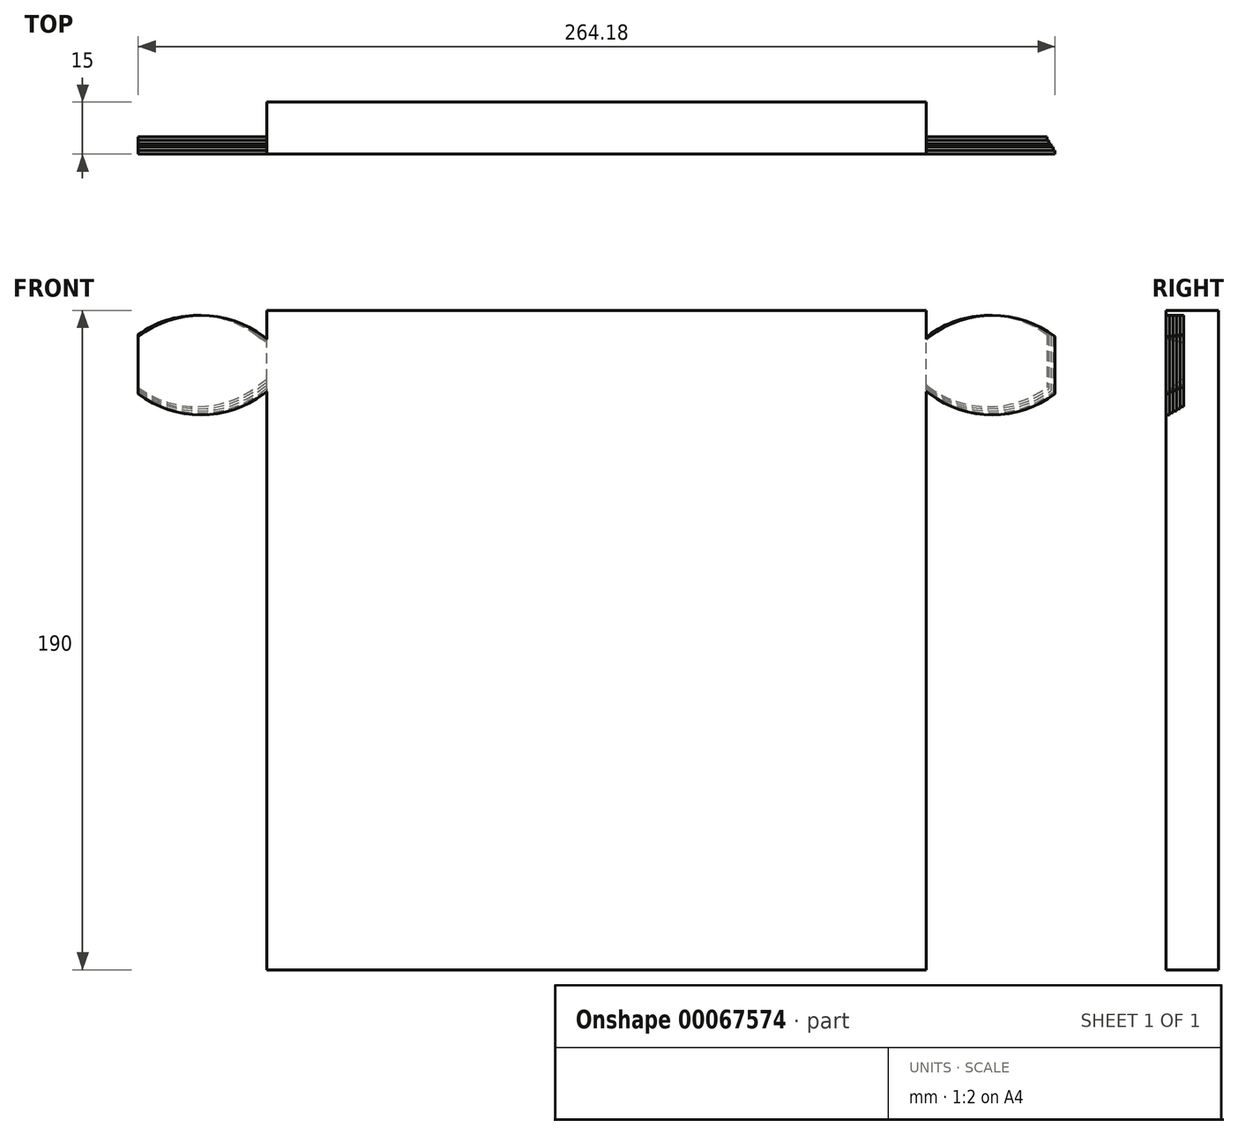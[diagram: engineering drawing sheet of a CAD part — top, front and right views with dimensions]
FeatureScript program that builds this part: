
annotation { "Feature Type Name" : "Feature", "Feature Type Description" : "" }
export const myFeature = defineFeature(function(context is Context, id is Id, definition is map)
    precondition{}
    {
        {
            var Q0;
            Q0=qCreatedBy(makeId("Front.planeOp"),FACE);
            var sketch = newSketch(context, id + "F0", { "sketchPlane" : qUnion([Q0])});
            skLineSegment(sketch, "E0.bottom", {"start": v(95, -95) * mm, "end": v(-95, -95) * mm});
            skLineSegment(sketch, "E0.top", {"start": v(95, 95) * mm, "end": v(-95, 95) * mm});
            skLineSegment(sketch, "E0.left", {"start": v(95, -95) * mm, "end": v(95, 95) * mm});
            skLineSegment(sketch, "E0.right", {"start": v(-95, -95) * mm, "end": v(-95, 95) * mm});
            skPoint(sketch, "E0.middle", {"position": v(0, 0) * mm});
            skSolve(sketch);
        }
        {
            var Q0;
            Q0=makeQuery(id+"F0.imprint","IMPRINT",FACE,{"disambiguationData":[TD([[makeQuery(id+"F0.imprint","IMPRINT",EDGE,{"derivedFrom":sQuery(id+"F0.wireOp",EDGE,"E0.bottom")}),-1.0]])]});
            extrude(context, id + "F1", {"entities" : qUnion([Q0]), "oppositeDirection" : true, "depth" : 15 * mm});
        }
        {
            var Q0;
            Q0=makeQuery(id+"F1.opExtrude","CAP_FACE",FACE,{"disambiguationData":[OSD([sQuery(id+"F0.wireOp",EDGE,"E0.bottom"),sQuery(id+"F0.wireOp",EDGE,"E0.top"),sQuery(id+"F0.wireOp",EDGE,"E0.left"),sQuery(id+"F0.wireOp",EDGE,"E0.right")])],"isStart":true});
            var sketch = newSketch(context, id + "F2", { "sketchPlane" : qUnion([Q0])});
            skLineSegment(sketch, "E1.bottom", {"start": v(-95, -95) * mm, "end": v(95, -95) * mm, "construction": true});
            skLineSegment(sketch, "E1.top", {"start": v(-95, 95) * mm, "end": v(95, 95) * mm, "construction": true});
            skLineSegment(sketch, "E1.left", {"start": v(-95, -95) * mm, "end": v(-95, 95) * mm, "construction": true});
            skLineSegment(sketch, "E1.right", {"start": v(95, -95) * mm, "end": v(95, 95) * mm, "construction": true});
            skPoint(sketch, "E1.middle", {"position": v(0, 0) * mm});
            skLineSegment(sketch, "E2", {"start": v(0, 95) * mm, "end": v(0, -95) * mm, "construction": true});
            skLineSegment(sketch, "E3", {"start": v(-95, 88.58) * mm, "end": v(95, 88.58) * mm, "construction": true});
            skArc(sketch, "E4", {"start": v(57, 88.58) * mm, "mid": v(76, 82.17) * mm, "end": v(95, 88.58) * mm, "construction": true});
            skArc(sketch, "E5", {"start": v(57, 88.58) * mm, "mid": v(38, 95) * mm, "end": v(19, 88.58) * mm, "construction": true});
            skArc(sketch, "E6", {"start": v(-19, 88.58) * mm, "mid": v(0, 82.17) * mm, "end": v(19, 88.58) * mm, "construction": true});
            skArc(sketch, "E7", {"start": v(-19, 88.58) * mm, "mid": v(-38, 95) * mm, "end": v(-57, 88.58) * mm, "construction": true});
            skArc(sketch, "E8", {"start": v(-95, 88.58) * mm, "mid": v(-76, 82.17) * mm, "end": v(-57, 88.58) * mm, "construction": true});
            skLineSegment(sketch, "E9", {"start": v(-95, 113.5) * mm, "end": v(95, 113.5) * mm, "construction": true});
            skLineSegment(sketch, "E10", {"start": v(-95, 63.66) * mm, "end": v(95, 63.66) * mm, "construction": true});
            skLineSegment(sketch, "E11", {"start": v(0, 113.5) * mm, "end": v(95, 88.58) * mm, "construction": true});
            skLineSegment(sketch, "E12", {"start": v(0, 88.58) * mm, "end": v(95, 63.66) * mm, "construction": true});
            skArc(sketch, "E13.1.0", {"start": v(-95, 88.58) * mm, "mid": v(-114, 95) * mm, "end": v(-133, 88.58) * mm, "construction": true});
            skPoint(sketch, "E13.center", {"position": v(-95, 88.58) * mm});
            skArc(sketch, "E14.1.0", {"start": v(133, 88.58) * mm, "mid": v(114, 95) * mm, "end": v(95, 88.58) * mm, "construction": true});
            skPoint(sketch, "E14.center", {"position": v(95, 88.58) * mm});
            skLineSegment(sketch, "E15", {"start": v(-95, 0) * mm, "end": v(95, 0) * mm, "construction": true});
            skLineSegment(sketch, "E16", {"start": v(-95, -79.17) * mm, "end": v(95, -79.17) * mm, "construction": true});
            skLineSegment(sketch, "E17", {"start": v(-95, -63.33) * mm, "end": v(95, -63.33) * mm, "construction": true});
            skLineSegment(sketch, "E18", {"start": v(-95, -47.5) * mm, "end": v(95, -47.5) * mm, "construction": true});
            skLineSegment(sketch, "E19", {"start": v(-95, -31.67) * mm, "end": v(95, -31.67) * mm, "construction": true});
            skLineSegment(sketch, "E20", {"start": v(-95, -15.83) * mm, "end": v(95, -15.83) * mm, "construction": true});
            skLineSegment(sketch, "E21", {"start": v(0, 0) * mm, "end": v(95, -15.83) * mm, "construction": true});
            skLineSegment(sketch, "E22", {"start": v(0, -15.83) * mm, "end": v(95, -31.67) * mm, "construction": true});
            skLineSegment(sketch, "E23", {"start": v(0, -31.67) * mm, "end": v(95, -47.5) * mm, "construction": true});
            skLineSegment(sketch, "E24", {"start": v(0, -47.5) * mm, "end": v(95, -63.33) * mm, "construction": true});
            skLineSegment(sketch, "E25", {"start": v(0, -63.33) * mm, "end": v(95, -79.17) * mm, "construction": true});
            skLineSegment(sketch, "E26", {"start": v(0, -79.17) * mm, "end": v(95, -95) * mm, "construction": true});
            skLineSegment(sketch, "E27", {"start": v(-76, 82.17) * mm, "end": v(-38, 82.17) * mm, "construction": true});
            skPoint(sketch, "E27.endSnap0", {"position": v(-38, 95) * mm});
            skLineSegment(sketch, "E28", {"start": v(-38, 82.17) * mm, "end": v(-38, 95) * mm, "construction": true});
            skLineSegment(sketch, "E29", {"start": v(-95, 0) * mm, "end": v(-95, -15.83) * mm, "construction": true});
            skLineSegment(sketch, "E30", {"start": v(-95, -12.83) * mm, "end": v(0, -12.83) * mm, "construction": true});
            skLineSegment(sketch, "E31", {"start": v(-47.5, -12.83) * mm, "end": v(-47.5, -15.83) * mm, "construction": true});
            skLineSegment(sketch, "E32", {"start": v(-47.5, -12.83) * mm, "end": v(-47.5, 0) * mm, "construction": true});
            skLineSegment(sketch, "E33", {"start": v(-95, 79.17) * mm, "end": v(95, 79.17) * mm, "construction": true});
            skPoint(sketch, "E34", {"position": v(38, 95) * mm});
            skArc(sketch, "E35.0", {"start": v(-94.1, 89.78) * mm, "mid": v(-114, 96.5) * mm, "end": v(-133.9, 89.78) * mm});
            skArc(sketch, "E35.1", {"start": v(-94.1, 89.78) * mm, "mid": v(-76, 83.67) * mm, "end": v(-57.9, 89.78) * mm});
            skArc(sketch, "E35.2", {"start": v(-18.1, 89.78) * mm, "mid": v(-38, 96.5) * mm, "end": v(-57.9, 89.78) * mm});
            skArc(sketch, "E35.3", {"start": v(133.9, 89.78) * mm, "mid": v(114, 96.5) * mm, "end": v(94.1, 89.78) * mm});
            skArc(sketch, "E35.4", {"start": v(57.9, 89.78) * mm, "mid": v(76, 83.67) * mm, "end": v(94.1, 89.78) * mm});
            skArc(sketch, "E35.5", {"start": v(57.9, 89.78) * mm, "mid": v(38, 96.5) * mm, "end": v(18.1, 89.78) * mm});
            skArc(sketch, "E35.6", {"start": v(-18.1, 89.78) * mm, "mid": v(0, 83.67) * mm, "end": v(18.1, 89.78) * mm});
            skArc(sketch, "E36.0", {"start": v(-95.9, 87.4) * mm, "mid": v(-114, 93.5) * mm, "end": v(-132.1, 87.4) * mm});
            skArc(sketch, "E36.1", {"start": v(-95.9, 87.4) * mm, "mid": v(-76, 80.67) * mm, "end": v(-56.1, 87.4) * mm});
            skArc(sketch, "E36.2", {"start": v(-19.9, 87.4) * mm, "mid": v(-38, 93.5) * mm, "end": v(-56.1, 87.4) * mm});
            skArc(sketch, "E36.3", {"start": v(132.1, 87.4) * mm, "mid": v(114, 93.5) * mm, "end": v(95.9, 87.4) * mm});
            skArc(sketch, "E36.4", {"start": v(56.1, 87.4) * mm, "mid": v(76, 80.67) * mm, "end": v(95.9, 87.4) * mm});
            skArc(sketch, "E36.5", {"start": v(56.1, 87.4) * mm, "mid": v(38, 93.5) * mm, "end": v(19.9, 87.4) * mm});
            skArc(sketch, "E36.6", {"start": v(-19.9, 87.4) * mm, "mid": v(0, 80.67) * mm, "end": v(19.9, 87.4) * mm});
            skArc(sketch, "E37.MirrorCS", {"start": v(-94.1, 68.56) * mm, "mid": v(-114, 61.83) * mm, "end": v(-133.9, 68.56) * mm});
            skArc(sketch, "E38.MirrorCS", {"start": v(-95.9, 70.94) * mm, "mid": v(-114, 64.83) * mm, "end": v(-132.1, 70.94) * mm});
            skArc(sketch, "E39.MirrorCS", {"start": v(-94.1, 68.56) * mm, "mid": v(-76, 74.67) * mm, "end": v(-57.9, 68.56) * mm});
            skArc(sketch, "E40.MirrorCS", {"start": v(-95.9, 70.94) * mm, "mid": v(-76, 77.67) * mm, "end": v(-56.1, 70.94) * mm});
            skArc(sketch, "E41.MirrorCS", {"start": v(-18.1, 68.56) * mm, "mid": v(-38, 61.83) * mm, "end": v(-57.9, 68.56) * mm});
            skArc(sketch, "E42.MirrorCS", {"start": v(-19.9, 70.94) * mm, "mid": v(-38, 64.83) * mm, "end": v(-56.1, 70.94) * mm});
            skArc(sketch, "E43.MirrorCS", {"start": v(-18.1, 68.56) * mm, "mid": v(0, 74.67) * mm, "end": v(18.1, 68.56) * mm});
            skArc(sketch, "E44.MirrorCS", {"start": v(-19.9, 70.94) * mm, "mid": v(0, 77.67) * mm, "end": v(19.9, 70.94) * mm});
            skArc(sketch, "E45.MirrorCS", {"start": v(57.9, 68.56) * mm, "mid": v(38, 61.83) * mm, "end": v(18.1, 68.56) * mm});
            skArc(sketch, "E46.MirrorCS", {"start": v(56.1, 70.94) * mm, "mid": v(38, 64.83) * mm, "end": v(19.9, 70.94) * mm});
            skArc(sketch, "E47.MirrorCS", {"start": v(57.9, 68.56) * mm, "mid": v(76, 74.67) * mm, "end": v(94.1, 68.56) * mm});
            skArc(sketch, "E48.MirrorCS", {"start": v(56.1, 70.94) * mm, "mid": v(76, 77.67) * mm, "end": v(95.9, 70.94) * mm});
            skArc(sketch, "E49.MirrorCS", {"start": v(133.9, 68.56) * mm, "mid": v(114, 61.83) * mm, "end": v(94.1, 68.56) * mm});
            skArc(sketch, "E50.MirrorCS", {"start": v(132.1, 70.94) * mm, "mid": v(114, 64.83) * mm, "end": v(95.9, 70.94) * mm});
            skArc(sketch, "E51.0.1.0", {"start": v(56.1, 33.6) * mm, "mid": v(76, 40.33) * mm, "end": v(95.9, 33.6) * mm});
            skArc(sketch, "E51.0.1.1", {"start": v(-94.1, 31.22) * mm, "mid": v(-114, 24.5) * mm, "end": v(-133.9, 31.22) * mm});
            skArc(sketch, "E51.0.1.2", {"start": v(57.9, 52.44) * mm, "mid": v(76, 46.33) * mm, "end": v(94.1, 52.44) * mm});
            skArc(sketch, "E51.0.1.3", {"start": v(-95.9, 50.05) * mm, "mid": v(-114, 56.16) * mm, "end": v(-132.1, 50.05) * mm});
            skArc(sketch, "E51.0.1.4", {"start": v(56.1, 50.05) * mm, "mid": v(38, 56.16) * mm, "end": v(19.9, 50.05) * mm});
            skArc(sketch, "E51.0.1.5", {"start": v(-95.9, 33.6) * mm, "mid": v(-76, 40.33) * mm, "end": v(-56.1, 33.6) * mm});
            skArc(sketch, "E51.0.1.6", {"start": v(-18.1, 52.44) * mm, "mid": v(0, 46.33) * mm, "end": v(18.1, 52.44) * mm});
            skArc(sketch, "E51.0.1.7", {"start": v(132.1, 33.6) * mm, "mid": v(114, 27.5) * mm, "end": v(95.9, 33.6) * mm});
            skArc(sketch, "E51.0.1.8", {"start": v(-19.9, 50.05) * mm, "mid": v(-38, 56.16) * mm, "end": v(-56.1, 50.05) * mm});
            skArc(sketch, "E51.0.1.9", {"start": v(-94.1, 52.44) * mm, "mid": v(-76, 46.33) * mm, "end": v(-57.9, 52.44) * mm});
            skArc(sketch, "E51.0.1.10", {"start": v(-18.1, 31.22) * mm, "mid": v(-38, 24.5) * mm, "end": v(-57.9, 31.22) * mm});
            skArc(sketch, "E51.0.1.11", {"start": v(-95.9, 33.6) * mm, "mid": v(-114, 27.5) * mm, "end": v(-132.1, 33.6) * mm});
            skArc(sketch, "E51.0.1.12", {"start": v(56.1, 50.05) * mm, "mid": v(76, 43.33) * mm, "end": v(95.9, 50.05) * mm});
            skArc(sketch, "E51.0.1.13", {"start": v(133.9, 52.44) * mm, "mid": v(114, 59.16) * mm, "end": v(94.1, 52.44) * mm});
            skArc(sketch, "E51.0.1.14", {"start": v(57.9, 31.22) * mm, "mid": v(76, 37.33) * mm, "end": v(94.1, 31.22) * mm});
            skArc(sketch, "E51.0.1.15", {"start": v(133.9, 31.22) * mm, "mid": v(114, 24.5) * mm, "end": v(94.1, 31.22) * mm});
            skArc(sketch, "E51.0.1.16", {"start": v(-94.1, 31.22) * mm, "mid": v(-76, 37.33) * mm, "end": v(-57.9, 31.22) * mm});
            skArc(sketch, "E51.0.1.17", {"start": v(-19.9, 50.05) * mm, "mid": v(0, 43.33) * mm, "end": v(19.9, 50.05) * mm});
            skArc(sketch, "E51.0.1.18", {"start": v(57.9, 52.44) * mm, "mid": v(38, 59.16) * mm, "end": v(18.1, 52.44) * mm});
            skArc(sketch, "E51.0.1.19", {"start": v(-95.9, 50.05) * mm, "mid": v(-76, 43.33) * mm, "end": v(-56.1, 50.05) * mm});
            skArc(sketch, "E51.0.1.20", {"start": v(-18.1, 31.22) * mm, "mid": v(0, 37.33) * mm, "end": v(18.1, 31.22) * mm});
            skArc(sketch, "E51.0.1.21", {"start": v(-94.1, 52.44) * mm, "mid": v(-114, 59.16) * mm, "end": v(-133.9, 52.44) * mm});
            skArc(sketch, "E51.0.1.22", {"start": v(-19.9, 33.6) * mm, "mid": v(0, 40.33) * mm, "end": v(19.9, 33.6) * mm});
            skArc(sketch, "E51.0.1.23", {"start": v(56.1, 33.6) * mm, "mid": v(38, 27.5) * mm, "end": v(19.9, 33.6) * mm});
            skArc(sketch, "E51.0.1.24", {"start": v(132.1, 50.05) * mm, "mid": v(114, 56.16) * mm, "end": v(95.9, 50.05) * mm});
            skArc(sketch, "E51.0.1.25", {"start": v(57.9, 31.22) * mm, "mid": v(38, 24.5) * mm, "end": v(18.1, 31.22) * mm});
            skArc(sketch, "E51.0.1.26", {"start": v(-18.1, 52.44) * mm, "mid": v(-38, 59.16) * mm, "end": v(-57.9, 52.44) * mm});
            skArc(sketch, "E51.0.1.27", {"start": v(-19.9, 33.6) * mm, "mid": v(-38, 27.5) * mm, "end": v(-56.1, 33.6) * mm});
            skArc(sketch, "E51.0.2.0", {"start": v(56.1, -3.73) * mm, "mid": v(76, 3) * mm, "end": v(95.9, -3.73) * mm});
            skArc(sketch, "E51.0.2.1", {"start": v(-94.1, -6.12) * mm, "mid": v(-114, -12.84) * mm, "end": v(-133.9, -6.12) * mm});
            skArc(sketch, "E51.0.2.2", {"start": v(57.9, 15.1) * mm, "mid": v(76, 9) * mm, "end": v(94.1, 15.1) * mm});
            skArc(sketch, "E51.0.2.3", {"start": v(-95.9, 12.71) * mm, "mid": v(-114, 18.82) * mm, "end": v(-132.1, 12.71) * mm});
            skArc(sketch, "E51.0.2.4", {"start": v(56.1, 12.71) * mm, "mid": v(38, 18.82) * mm, "end": v(19.9, 12.71) * mm});
            skArc(sketch, "E51.0.2.5", {"start": v(-95.9, -3.73) * mm, "mid": v(-76, 3) * mm, "end": v(-56.1, -3.73) * mm});
            skArc(sketch, "E51.0.2.6", {"start": v(-18.1, 15.1) * mm, "mid": v(0, 9) * mm, "end": v(18.1, 15.1) * mm});
            skArc(sketch, "E51.0.2.7", {"start": v(132.1, -3.73) * mm, "mid": v(114, -9.84) * mm, "end": v(95.9, -3.73) * mm});
            skArc(sketch, "E51.0.2.8", {"start": v(-19.9, 12.71) * mm, "mid": v(-38, 18.82) * mm, "end": v(-56.1, 12.71) * mm});
            skArc(sketch, "E51.0.2.9", {"start": v(-94.1, 15.1) * mm, "mid": v(-76, 9) * mm, "end": v(-57.9, 15.1) * mm});
            skArc(sketch, "E51.0.2.10", {"start": v(-18.1, -6.12) * mm, "mid": v(-38, -12.84) * mm, "end": v(-57.9, -6.12) * mm});
            skArc(sketch, "E51.0.2.11", {"start": v(-95.9, -3.73) * mm, "mid": v(-114, -9.84) * mm, "end": v(-132.1, -3.73) * mm});
            skArc(sketch, "E51.0.2.12", {"start": v(56.1, 12.71) * mm, "mid": v(76, 6) * mm, "end": v(95.9, 12.71) * mm});
            skArc(sketch, "E51.0.2.13", {"start": v(133.9, 15.1) * mm, "mid": v(114, 21.82) * mm, "end": v(94.1, 15.1) * mm});
            skArc(sketch, "E51.0.2.14", {"start": v(57.9, -6.12) * mm, "mid": v(76, 0) * mm, "end": v(94.1, -6.12) * mm});
            skArc(sketch, "E51.0.2.15", {"start": v(133.9, -6.12) * mm, "mid": v(114, -12.84) * mm, "end": v(94.1, -6.12) * mm});
            skArc(sketch, "E51.0.2.16", {"start": v(-94.1, -6.12) * mm, "mid": v(-76, 0) * mm, "end": v(-57.9, -6.12) * mm});
            skArc(sketch, "E51.0.2.17", {"start": v(-19.9, 12.71) * mm, "mid": v(0, 6) * mm, "end": v(19.9, 12.71) * mm});
            skArc(sketch, "E51.0.2.18", {"start": v(57.9, 15.1) * mm, "mid": v(38, 21.82) * mm, "end": v(18.1, 15.1) * mm});
            skArc(sketch, "E51.0.2.19", {"start": v(-95.9, 12.71) * mm, "mid": v(-76, 6) * mm, "end": v(-56.1, 12.71) * mm});
            skArc(sketch, "E51.0.2.20", {"start": v(-18.1, -6.12) * mm, "mid": v(0, 0) * mm, "end": v(18.1, -6.12) * mm});
            skArc(sketch, "E51.0.2.21", {"start": v(-94.1, 15.1) * mm, "mid": v(-114, 21.82) * mm, "end": v(-133.9, 15.1) * mm});
            skArc(sketch, "E51.0.2.22", {"start": v(-19.9, -3.73) * mm, "mid": v(0, 3) * mm, "end": v(19.9, -3.73) * mm});
            skArc(sketch, "E51.0.2.23", {"start": v(56.1, -3.73) * mm, "mid": v(38, -9.84) * mm, "end": v(19.9, -3.73) * mm});
            skArc(sketch, "E51.0.2.24", {"start": v(132.1, 12.71) * mm, "mid": v(114, 18.82) * mm, "end": v(95.9, 12.71) * mm});
            skArc(sketch, "E51.0.2.25", {"start": v(57.9, -6.12) * mm, "mid": v(38, -12.84) * mm, "end": v(18.1, -6.12) * mm});
            skArc(sketch, "E51.0.2.26", {"start": v(-18.1, 15.1) * mm, "mid": v(-38, 21.82) * mm, "end": v(-57.9, 15.1) * mm});
            skArc(sketch, "E51.0.2.27", {"start": v(-19.9, -3.73) * mm, "mid": v(-38, -9.84) * mm, "end": v(-56.1, -3.73) * mm});
            skArc(sketch, "E51.0.3.0", {"start": v(56.1, -41.07) * mm, "mid": v(76, -34.35) * mm, "end": v(95.9, -41.07) * mm});
            skArc(sketch, "E51.0.3.1", {"start": v(-94.1, -43.46) * mm, "mid": v(-114, -50.18) * mm, "end": v(-133.9, -43.46) * mm});
            skArc(sketch, "E51.0.3.2", {"start": v(57.9, -22.24) * mm, "mid": v(76, -28.35) * mm, "end": v(94.1, -22.24) * mm});
            skArc(sketch, "E51.0.3.3", {"start": v(-95.9, -24.62) * mm, "mid": v(-114, -18.51) * mm, "end": v(-132.1, -24.62) * mm});
            skArc(sketch, "E51.0.3.4", {"start": v(56.1, -24.62) * mm, "mid": v(38, -18.51) * mm, "end": v(19.9, -24.62) * mm});
            skArc(sketch, "E51.0.3.5", {"start": v(-95.9, -41.07) * mm, "mid": v(-76, -34.35) * mm, "end": v(-56.1, -41.07) * mm});
            skArc(sketch, "E51.0.3.6", {"start": v(-18.1, -22.24) * mm, "mid": v(0, -28.35) * mm, "end": v(18.1, -22.24) * mm});
            skArc(sketch, "E51.0.3.7", {"start": v(132.1, -41.07) * mm, "mid": v(114, -47.18) * mm, "end": v(95.9, -41.07) * mm});
            skArc(sketch, "E51.0.3.8", {"start": v(-19.9, -24.62) * mm, "mid": v(-38, -18.51) * mm, "end": v(-56.1, -24.62) * mm});
            skArc(sketch, "E51.0.3.9", {"start": v(-94.1, -22.24) * mm, "mid": v(-76, -28.35) * mm, "end": v(-57.9, -22.24) * mm});
            skArc(sketch, "E51.0.3.10", {"start": v(-18.1, -43.46) * mm, "mid": v(-38, -50.18) * mm, "end": v(-57.9, -43.46) * mm});
            skArc(sketch, "E51.0.3.11", {"start": v(-95.9, -41.07) * mm, "mid": v(-114, -47.18) * mm, "end": v(-132.1, -41.07) * mm});
            skArc(sketch, "E51.0.3.12", {"start": v(56.1, -24.62) * mm, "mid": v(76, -31.35) * mm, "end": v(95.9, -24.62) * mm});
            skArc(sketch, "E51.0.3.13", {"start": v(133.9, -22.24) * mm, "mid": v(114, -15.51) * mm, "end": v(94.1, -22.24) * mm});
            skArc(sketch, "E51.0.3.14", {"start": v(57.9, -43.46) * mm, "mid": v(76, -37.35) * mm, "end": v(94.1, -43.46) * mm});
            skArc(sketch, "E51.0.3.15", {"start": v(133.9, -43.46) * mm, "mid": v(114, -50.18) * mm, "end": v(94.1, -43.46) * mm});
            skArc(sketch, "E51.0.3.16", {"start": v(-94.1, -43.46) * mm, "mid": v(-76, -37.35) * mm, "end": v(-57.9, -43.46) * mm});
            skArc(sketch, "E51.0.3.17", {"start": v(-19.9, -24.62) * mm, "mid": v(0, -31.35) * mm, "end": v(19.9, -24.62) * mm});
            skArc(sketch, "E51.0.3.18", {"start": v(57.9, -22.24) * mm, "mid": v(38, -15.51) * mm, "end": v(18.1, -22.24) * mm});
            skArc(sketch, "E51.0.3.19", {"start": v(-95.9, -24.62) * mm, "mid": v(-76, -31.35) * mm, "end": v(-56.1, -24.62) * mm});
            skArc(sketch, "E51.0.3.20", {"start": v(-18.1, -43.46) * mm, "mid": v(0, -37.35) * mm, "end": v(18.1, -43.46) * mm});
            skArc(sketch, "E51.0.3.21", {"start": v(-94.1, -22.24) * mm, "mid": v(-114, -15.51) * mm, "end": v(-133.9, -22.24) * mm});
            skArc(sketch, "E51.0.3.22", {"start": v(-19.9, -41.07) * mm, "mid": v(0, -34.35) * mm, "end": v(19.9, -41.07) * mm});
            skArc(sketch, "E51.0.3.23", {"start": v(56.1, -41.07) * mm, "mid": v(38, -47.18) * mm, "end": v(19.9, -41.07) * mm});
            skArc(sketch, "E51.0.3.24", {"start": v(132.1, -24.62) * mm, "mid": v(114, -18.51) * mm, "end": v(95.9, -24.62) * mm});
            skArc(sketch, "E51.0.3.25", {"start": v(57.9, -43.46) * mm, "mid": v(38, -50.18) * mm, "end": v(18.1, -43.46) * mm});
            skArc(sketch, "E51.0.3.26", {"start": v(-18.1, -22.24) * mm, "mid": v(-38, -15.51) * mm, "end": v(-57.9, -22.24) * mm});
            skArc(sketch, "E51.0.3.27", {"start": v(-19.9, -41.07) * mm, "mid": v(-38, -47.18) * mm, "end": v(-56.1, -41.07) * mm});
            skArc(sketch, "E51.0.4.0", {"start": v(56.1, -78.4) * mm, "mid": v(76, -71.69) * mm, "end": v(95.9, -78.4) * mm});
            skArc(sketch, "E51.0.4.1", {"start": v(-94.1, -80.8) * mm, "mid": v(-114, -87.52) * mm, "end": v(-133.9, -80.8) * mm});
            skArc(sketch, "E51.0.4.2", {"start": v(57.9, -59.58) * mm, "mid": v(76, -65.69) * mm, "end": v(94.1, -59.58) * mm});
            skArc(sketch, "E51.0.4.3", {"start": v(-95.9, -61.96) * mm, "mid": v(-114, -55.85) * mm, "end": v(-132.1, -61.96) * mm});
            skArc(sketch, "E51.0.4.4", {"start": v(56.1, -61.96) * mm, "mid": v(38, -55.85) * mm, "end": v(19.9, -61.96) * mm});
            skArc(sketch, "E51.0.4.5", {"start": v(-95.9, -78.4) * mm, "mid": v(-76, -71.69) * mm, "end": v(-56.1, -78.4) * mm});
            skArc(sketch, "E51.0.4.6", {"start": v(-18.1, -59.58) * mm, "mid": v(0, -65.69) * mm, "end": v(18.1, -59.58) * mm});
            skArc(sketch, "E51.0.4.7", {"start": v(132.1, -78.4) * mm, "mid": v(114, -84.52) * mm, "end": v(95.9, -78.4) * mm});
            skArc(sketch, "E51.0.4.8", {"start": v(-19.9, -61.96) * mm, "mid": v(-38, -55.85) * mm, "end": v(-56.1, -61.96) * mm});
            skArc(sketch, "E51.0.4.9", {"start": v(-94.1, -59.58) * mm, "mid": v(-76, -65.69) * mm, "end": v(-57.9, -59.58) * mm});
            skArc(sketch, "E51.0.4.10", {"start": v(-18.1, -80.8) * mm, "mid": v(-38, -87.52) * mm, "end": v(-57.9, -80.8) * mm});
            skArc(sketch, "E51.0.4.11", {"start": v(-95.9, -78.4) * mm, "mid": v(-114, -84.52) * mm, "end": v(-132.1, -78.4) * mm});
            skArc(sketch, "E51.0.4.12", {"start": v(56.1, -61.96) * mm, "mid": v(76, -68.69) * mm, "end": v(95.9, -61.96) * mm});
            skArc(sketch, "E51.0.4.13", {"start": v(133.9, -59.58) * mm, "mid": v(114, -52.85) * mm, "end": v(94.1, -59.58) * mm});
            skArc(sketch, "E51.0.4.14", {"start": v(57.9, -80.8) * mm, "mid": v(76, -74.69) * mm, "end": v(94.1, -80.8) * mm});
            skArc(sketch, "E51.0.4.15", {"start": v(133.9, -80.8) * mm, "mid": v(114, -87.52) * mm, "end": v(94.1, -80.8) * mm});
            skArc(sketch, "E51.0.4.16", {"start": v(-94.1, -80.8) * mm, "mid": v(-76, -74.69) * mm, "end": v(-57.9, -80.8) * mm});
            skArc(sketch, "E51.0.4.17", {"start": v(-19.9, -61.96) * mm, "mid": v(0, -68.69) * mm, "end": v(19.9, -61.96) * mm});
            skArc(sketch, "E51.0.4.18", {"start": v(57.9, -59.58) * mm, "mid": v(38, -52.85) * mm, "end": v(18.1, -59.58) * mm});
            skArc(sketch, "E51.0.4.19", {"start": v(-95.9, -61.96) * mm, "mid": v(-76, -68.69) * mm, "end": v(-56.1, -61.96) * mm});
            skArc(sketch, "E51.0.4.20", {"start": v(-18.1, -80.8) * mm, "mid": v(0, -74.69) * mm, "end": v(18.1, -80.8) * mm});
            skArc(sketch, "E51.0.4.21", {"start": v(-94.1, -59.58) * mm, "mid": v(-114, -52.85) * mm, "end": v(-133.9, -59.58) * mm});
            skArc(sketch, "E51.0.4.22", {"start": v(-19.9, -78.4) * mm, "mid": v(0, -71.69) * mm, "end": v(19.9, -78.4) * mm});
            skArc(sketch, "E51.0.4.23", {"start": v(56.1, -78.4) * mm, "mid": v(38, -84.52) * mm, "end": v(19.9, -78.4) * mm});
            skArc(sketch, "E51.0.4.24", {"start": v(132.1, -61.96) * mm, "mid": v(114, -55.85) * mm, "end": v(95.9, -61.96) * mm});
            skArc(sketch, "E51.0.4.25", {"start": v(57.9, -80.8) * mm, "mid": v(38, -87.52) * mm, "end": v(18.1, -80.8) * mm});
            skArc(sketch, "E51.0.4.26", {"start": v(-18.1, -59.58) * mm, "mid": v(-38, -52.85) * mm, "end": v(-57.9, -59.58) * mm});
            skArc(sketch, "E51.0.4.27", {"start": v(-19.9, -78.4) * mm, "mid": v(-38, -84.52) * mm, "end": v(-56.1, -78.4) * mm});
            skArc(sketch, "E51.0.5.0", {"start": v(56.1, -115.75) * mm, "mid": v(76, -109.02) * mm, "end": v(95.9, -115.75) * mm});
            skArc(sketch, "E51.0.5.1", {"start": v(-94.1, -118.13) * mm, "mid": v(-114, -124.86) * mm, "end": v(-133.9, -118.13) * mm});
            skArc(sketch, "E51.0.5.2", {"start": v(57.9, -96.91) * mm, "mid": v(76, -103.02) * mm, "end": v(94.1, -96.91) * mm});
            skArc(sketch, "E51.0.5.3", {"start": v(-95.9, -99.3) * mm, "mid": v(-114, -93.2) * mm, "end": v(-132.1, -99.3) * mm});
            skArc(sketch, "E51.0.5.4", {"start": v(56.1, -99.3) * mm, "mid": v(38, -93.2) * mm, "end": v(19.9, -99.3) * mm});
            skArc(sketch, "E51.0.5.5", {"start": v(-95.9, -115.75) * mm, "mid": v(-76, -109.02) * mm, "end": v(-56.1, -115.75) * mm});
            skArc(sketch, "E51.0.5.6", {"start": v(-18.1, -96.91) * mm, "mid": v(0, -103.02) * mm, "end": v(18.1, -96.91) * mm});
            skArc(sketch, "E51.0.5.7", {"start": v(132.1, -115.75) * mm, "mid": v(114, -121.86) * mm, "end": v(95.9, -115.75) * mm});
            skArc(sketch, "E51.0.5.8", {"start": v(-19.9, -99.3) * mm, "mid": v(-38, -93.2) * mm, "end": v(-56.1, -99.3) * mm});
            skArc(sketch, "E51.0.5.9", {"start": v(-94.1, -96.91) * mm, "mid": v(-76, -103.02) * mm, "end": v(-57.9, -96.91) * mm});
            skArc(sketch, "E51.0.5.10", {"start": v(-18.1, -118.13) * mm, "mid": v(-38, -124.86) * mm, "end": v(-57.9, -118.13) * mm});
            skArc(sketch, "E51.0.5.11", {"start": v(-95.9, -115.75) * mm, "mid": v(-114, -121.86) * mm, "end": v(-132.1, -115.75) * mm});
            skArc(sketch, "E51.0.5.12", {"start": v(56.1, -99.3) * mm, "mid": v(76, -106.02) * mm, "end": v(95.9, -99.3) * mm});
            skArc(sketch, "E51.0.5.13", {"start": v(133.9, -96.91) * mm, "mid": v(114, -90.2) * mm, "end": v(94.1, -96.91) * mm});
            skArc(sketch, "E51.0.5.14", {"start": v(57.9, -118.13) * mm, "mid": v(76, -112.02) * mm, "end": v(94.1, -118.13) * mm});
            skArc(sketch, "E51.0.5.15", {"start": v(133.9, -118.13) * mm, "mid": v(114, -124.86) * mm, "end": v(94.1, -118.13) * mm});
            skArc(sketch, "E51.0.5.16", {"start": v(-94.1, -118.13) * mm, "mid": v(-76, -112.02) * mm, "end": v(-57.9, -118.13) * mm});
            skArc(sketch, "E51.0.5.17", {"start": v(-19.9, -99.3) * mm, "mid": v(0, -106.02) * mm, "end": v(19.9, -99.3) * mm});
            skArc(sketch, "E51.0.5.18", {"start": v(57.9, -96.91) * mm, "mid": v(38, -90.2) * mm, "end": v(18.1, -96.91) * mm});
            skArc(sketch, "E51.0.5.19", {"start": v(-95.9, -99.3) * mm, "mid": v(-76, -106.02) * mm, "end": v(-56.1, -99.3) * mm});
            skArc(sketch, "E51.0.5.20", {"start": v(-18.1, -118.13) * mm, "mid": v(0, -112.02) * mm, "end": v(18.1, -118.13) * mm});
            skArc(sketch, "E51.0.5.21", {"start": v(-94.1, -96.91) * mm, "mid": v(-114, -90.2) * mm, "end": v(-133.9, -96.91) * mm});
            skArc(sketch, "E51.0.5.22", {"start": v(-19.9, -115.75) * mm, "mid": v(0, -109.02) * mm, "end": v(19.9, -115.75) * mm});
            skArc(sketch, "E51.0.5.23", {"start": v(56.1, -115.75) * mm, "mid": v(38, -121.86) * mm, "end": v(19.9, -115.75) * mm});
            skArc(sketch, "E51.0.5.24", {"start": v(132.1, -99.3) * mm, "mid": v(114, -93.2) * mm, "end": v(95.9, -99.3) * mm});
            skArc(sketch, "E51.0.5.25", {"start": v(57.9, -118.13) * mm, "mid": v(38, -124.86) * mm, "end": v(18.1, -118.13) * mm});
            skArc(sketch, "E51.0.5.26", {"start": v(-18.1, -96.91) * mm, "mid": v(-38, -90.2) * mm, "end": v(-57.9, -96.91) * mm});
            skArc(sketch, "E51.0.5.27", {"start": v(-19.9, -115.75) * mm, "mid": v(-38, -121.86) * mm, "end": v(-56.1, -115.75) * mm});
            skLineSegment(sketch, "E51.direction1", {"start": v(-133.9, 89.78) * mm, "end": v(226.64, 89.78) * mm, "construction": true});
            skLineSegment(sketch, "E51.direction2", {"start": v(-133.9, 89.78) * mm, "end": v(-133.9, 52.44) * mm, "construction": true});
            skLineSegment(sketch, "E52", {"start": v(-132.1, 87.4) * mm, "end": v(-132.1, 70.94) * mm});
            skLineSegment(sketch, "E53", {"start": v(132.1, 87.4) * mm, "end": v(132.1, 70.94) * mm});
            skSolve(sketch);
        }
        {
            var Q0;
            Q0 = qSketchRegion(id + "F2", true);
            extrude(context, id + "F3", {"entities" : qUnion([Q0]), "oppositeDirection" : true, "depth" : 1 * mm});
        }
        {
            var Q0;
            Q0=makeQuery(id+"F3.opExtrude","CAP_FACE",FACE,{"disambiguationData":[OSD([sQuery(id+"F2.wireOp",EDGE,"E36.0"),sQuery(id+"F2.wireOp",EDGE,"E36.1"),sQuery(id+"F2.wireOp",EDGE,"E36.2"),sQuery(id+"F2.wireOp",EDGE,"E36.3"),sQuery(id+"F2.wireOp",EDGE,"E36.4"),sQuery(id+"F2.wireOp",EDGE,"E36.5"),sQuery(id+"F2.wireOp",EDGE,"E36.6"),sQuery(id+"F2.wireOp",EDGE,"E38.MirrorCS"),sQuery(id+"F2.wireOp",EDGE,"E40.MirrorCS"),sQuery(id+"F2.wireOp",EDGE,"E42.MirrorCS"),sQuery(id+"F2.wireOp",EDGE,"E44.MirrorCS"),sQuery(id+"F2.wireOp",EDGE,"E46.MirrorCS"),sQuery(id+"F2.wireOp",EDGE,"E48.MirrorCS"),sQuery(id+"F2.wireOp",EDGE,"E50.MirrorCS"),sQuery(id+"F2.wireOp",EDGE,"E52"),sQuery(id+"F2.wireOp",EDGE,"E53")])],"isStart":false});
            var sketch = newSketch(context, id + "F4", { "sketchPlane" : qUnion([Q0])});
            skArc(sketch, "E54.0", {"start": v(-131.8, 87.24) * mm, "mid": v(-113.93, 93.2) * mm, "end": v(-96.1, 87.15) * mm, "construction": true});
            skArc(sketch, "E54.1", {"start": v(-55.9, 87.15) * mm, "mid": v(-76, 80.37) * mm, "end": v(-96.1, 87.15) * mm, "construction": true});
            skArc(sketch, "E54.2", {"start": v(-55.9, 87.15) * mm, "mid": v(-38, 93.2) * mm, "end": v(-20.1, 87.15) * mm, "construction": true});
            skArc(sketch, "E54.3", {"start": v(20.1, 87.15) * mm, "mid": v(0, 80.37) * mm, "end": v(-20.1, 87.15) * mm, "construction": true});
            skArc(sketch, "E54.4", {"start": v(20.1, 87.15) * mm, "mid": v(38, 93.2) * mm, "end": v(55.9, 87.15) * mm, "construction": true});
            skArc(sketch, "E54.5", {"start": v(20.1, 71.18) * mm, "mid": v(0, 77.97) * mm, "end": v(-20.1, 71.18) * mm, "construction": true});
            skArc(sketch, "E54.6", {"start": v(-55.9, 71.18) * mm, "mid": v(-38, 65.13) * mm, "end": v(-20.1, 71.18) * mm, "construction": true});
            skArc(sketch, "E54.7", {"start": v(-55.9, 71.18) * mm, "mid": v(-76, 77.97) * mm, "end": v(-96.1, 71.18) * mm, "construction": true});
            skArc(sketch, "E54.8", {"start": v(-131.8, 71.1) * mm, "mid": v(-113.93, 65.13) * mm, "end": v(-96.1, 71.18) * mm, "construction": true});
            skArc(sketch, "E54.9", {"start": v(20.1, 71.18) * mm, "mid": v(38, 65.13) * mm, "end": v(55.9, 71.18) * mm, "construction": true});
            skArc(sketch, "E54.10", {"start": v(96.1, 71.18) * mm, "mid": v(76, 77.97) * mm, "end": v(55.9, 71.18) * mm, "construction": true});
            skArc(sketch, "E54.11", {"start": v(96.1, 71.18) * mm, "mid": v(113.93, 65.13) * mm, "end": v(131.8, 71.1) * mm, "construction": true});
            skLineSegment(sketch, "E54.12", {"start": v(131.8, 87.24) * mm, "end": v(131.8, 71.1) * mm, "construction": true});
            skArc(sketch, "E54.13", {"start": v(96.1, 87.15) * mm, "mid": v(113.93, 93.2) * mm, "end": v(131.8, 87.24) * mm, "construction": true});
            skLineSegment(sketch, "E54.14", {"start": v(-131.8, 87.24) * mm, "end": v(-131.8, 71.1) * mm, "construction": true});
            skArc(sketch, "E54.15", {"start": v(96.1, 87.15) * mm, "mid": v(76, 80.37) * mm, "end": v(55.9, 87.15) * mm, "construction": true});
            skArc(sketch, "E55.0.1.0", {"start": v(-131.8, 87.54) * mm, "mid": v(-113.93, 93.5) * mm, "end": v(-96.1, 87.45) * mm, "construction": true});
            skArc(sketch, "E55.0.1.1", {"start": v(96.1, 87.45) * mm, "mid": v(113.93, 93.5) * mm, "end": v(131.8, 87.54) * mm, "construction": true});
            skArc(sketch, "E55.0.1.2", {"start": v(20.1, 71.48) * mm, "mid": v(0, 78.27) * mm, "end": v(-20.1, 71.48) * mm, "construction": true});
            skArc(sketch, "E55.0.1.3", {"start": v(96.1, 71.48) * mm, "mid": v(76, 78.27) * mm, "end": v(55.9, 71.48) * mm, "construction": true});
            skArc(sketch, "E55.0.1.4", {"start": v(96.1, 87.45) * mm, "mid": v(76, 80.67) * mm, "end": v(55.9, 87.45) * mm, "construction": true});
            skArc(sketch, "E55.0.1.5", {"start": v(20.1, 87.45) * mm, "mid": v(38, 93.5) * mm, "end": v(55.9, 87.45) * mm, "construction": true});
            skLineSegment(sketch, "E55.0.1.6", {"start": v(131.8, 87.54) * mm, "end": v(131.8, 71.4) * mm, "construction": true});
            skArc(sketch, "E55.0.1.7", {"start": v(20.1, 71.48) * mm, "mid": v(38, 65.43) * mm, "end": v(55.9, 71.48) * mm, "construction": true});
            skArc(sketch, "E55.0.1.8", {"start": v(20.1, 87.45) * mm, "mid": v(0, 80.67) * mm, "end": v(-20.1, 87.45) * mm, "construction": true});
            skArc(sketch, "E55.0.1.9", {"start": v(-131.8, 71.4) * mm, "mid": v(-113.93, 65.43) * mm, "end": v(-96.1, 71.48) * mm, "construction": true});
            skLineSegment(sketch, "E55.0.1.10", {"start": v(-131.8, 87.54) * mm, "end": v(-131.8, 71.4) * mm, "construction": true});
            skArc(sketch, "E55.0.1.11", {"start": v(-55.9, 87.45) * mm, "mid": v(-38, 93.5) * mm, "end": v(-20.1, 87.45) * mm, "construction": true});
            skArc(sketch, "E55.0.1.12", {"start": v(-55.9, 71.48) * mm, "mid": v(-76, 78.27) * mm, "end": v(-96.1, 71.48) * mm, "construction": true});
            skArc(sketch, "E55.0.1.13", {"start": v(-55.9, 87.45) * mm, "mid": v(-76, 80.67) * mm, "end": v(-96.1, 87.45) * mm, "construction": true});
            skArc(sketch, "E55.0.1.14", {"start": v(96.1, 71.48) * mm, "mid": v(113.93, 65.43) * mm, "end": v(131.8, 71.4) * mm, "construction": true});
            skArc(sketch, "E55.0.1.15", {"start": v(-55.9, 71.48) * mm, "mid": v(-38, 65.43) * mm, "end": v(-20.1, 71.48) * mm, "construction": true});
            skArc(sketch, "E55.1.0.0", {"start": v(-131.5, 87.24) * mm, "mid": v(-113.63, 93.2) * mm, "end": v(-95.8, 87.15) * mm, "construction": true});
            skArc(sketch, "E55.1.0.1", {"start": v(96.4, 87.15) * mm, "mid": v(114.23, 93.2) * mm, "end": v(132.1, 87.24) * mm, "construction": true});
            skArc(sketch, "E55.1.0.2", {"start": v(20.4, 71.18) * mm, "mid": v(0.3, 77.97) * mm, "end": v(-19.8, 71.18) * mm, "construction": true});
            skArc(sketch, "E55.1.0.3", {"start": v(96.4, 71.18) * mm, "mid": v(76.3, 77.97) * mm, "end": v(56.2, 71.18) * mm, "construction": true});
            skArc(sketch, "E55.1.0.4", {"start": v(96.4, 87.15) * mm, "mid": v(76.3, 80.37) * mm, "end": v(56.2, 87.15) * mm, "construction": true});
            skArc(sketch, "E55.1.0.5", {"start": v(20.4, 87.15) * mm, "mid": v(38.3, 93.2) * mm, "end": v(56.2, 87.15) * mm, "construction": true});
            skLineSegment(sketch, "E55.1.0.6", {"start": v(132.1, 87.24) * mm, "end": v(132.1, 71.1) * mm, "construction": true});
            skArc(sketch, "E55.1.0.7", {"start": v(20.4, 71.18) * mm, "mid": v(38.3, 65.13) * mm, "end": v(56.2, 71.18) * mm, "construction": true});
            skArc(sketch, "E55.1.0.8", {"start": v(20.4, 87.15) * mm, "mid": v(0.3, 80.37) * mm, "end": v(-19.8, 87.15) * mm, "construction": true});
            skArc(sketch, "E55.1.0.9", {"start": v(-131.5, 71.1) * mm, "mid": v(-113.63, 65.13) * mm, "end": v(-95.8, 71.18) * mm, "construction": true});
            skLineSegment(sketch, "E55.1.0.10", {"start": v(-131.5, 87.24) * mm, "end": v(-131.5, 71.1) * mm, "construction": true});
            skArc(sketch, "E55.1.0.11", {"start": v(-55.6, 87.15) * mm, "mid": v(-37.7, 93.2) * mm, "end": v(-19.8, 87.15) * mm, "construction": true});
            skArc(sketch, "E55.1.0.12", {"start": v(-55.6, 71.18) * mm, "mid": v(-75.7, 77.97) * mm, "end": v(-95.8, 71.18) * mm, "construction": true});
            skArc(sketch, "E55.1.0.13", {"start": v(-55.6, 87.15) * mm, "mid": v(-75.7, 80.37) * mm, "end": v(-95.8, 87.15) * mm, "construction": true});
            skArc(sketch, "E55.1.0.14", {"start": v(96.4, 71.18) * mm, "mid": v(114.23, 65.13) * mm, "end": v(132.1, 71.1) * mm, "construction": true});
            skArc(sketch, "E55.1.0.15", {"start": v(-55.6, 71.18) * mm, "mid": v(-37.7, 65.13) * mm, "end": v(-19.8, 71.18) * mm, "construction": true});
            skArc(sketch, "E55.1.1.0", {"start": v(-131.5, 87.54) * mm, "mid": v(-113.63, 93.5) * mm, "end": v(-95.8, 87.45) * mm});
            skArc(sketch, "E55.1.1.1", {"start": v(96.4, 87.45) * mm, "mid": v(114.23, 93.5) * mm, "end": v(132.1, 87.54) * mm});
            skArc(sketch, "E55.1.1.2", {"start": v(20.4, 71.48) * mm, "mid": v(0.3, 78.27) * mm, "end": v(-19.8, 71.48) * mm});
            skArc(sketch, "E55.1.1.3", {"start": v(96.4, 71.48) * mm, "mid": v(76.3, 78.27) * mm, "end": v(56.2, 71.48) * mm});
            skArc(sketch, "E55.1.1.4", {"start": v(96.4, 87.45) * mm, "mid": v(76.3, 80.67) * mm, "end": v(56.2, 87.45) * mm});
            skArc(sketch, "E55.1.1.5", {"start": v(20.4, 87.45) * mm, "mid": v(38.3, 93.5) * mm, "end": v(56.2, 87.45) * mm});
            skLineSegment(sketch, "E55.1.1.6", {"start": v(132.1, 87.54) * mm, "end": v(132.1, 71.4) * mm});
            skArc(sketch, "E55.1.1.7", {"start": v(20.4, 71.48) * mm, "mid": v(38.3, 65.43) * mm, "end": v(56.2, 71.48) * mm});
            skArc(sketch, "E55.1.1.8", {"start": v(20.4, 87.45) * mm, "mid": v(0.3, 80.67) * mm, "end": v(-19.8, 87.45) * mm});
            skArc(sketch, "E55.1.1.9", {"start": v(-131.5, 71.4) * mm, "mid": v(-113.63, 65.43) * mm, "end": v(-95.8, 71.48) * mm});
            skLineSegment(sketch, "E55.1.1.10", {"start": v(-131.5, 87.54) * mm, "end": v(-131.5, 71.4) * mm});
            skArc(sketch, "E55.1.1.11", {"start": v(-55.6, 87.45) * mm, "mid": v(-37.7, 93.5) * mm, "end": v(-19.8, 87.45) * mm});
            skArc(sketch, "E55.1.1.12", {"start": v(-55.6, 71.48) * mm, "mid": v(-75.7, 78.27) * mm, "end": v(-95.8, 71.48) * mm});
            skArc(sketch, "E55.1.1.13", {"start": v(-55.6, 87.45) * mm, "mid": v(-75.7, 80.67) * mm, "end": v(-95.8, 87.45) * mm});
            skArc(sketch, "E55.1.1.14", {"start": v(96.4, 71.48) * mm, "mid": v(114.23, 65.43) * mm, "end": v(132.1, 71.4) * mm});
            skArc(sketch, "E55.1.1.15", {"start": v(-55.6, 71.48) * mm, "mid": v(-37.7, 65.43) * mm, "end": v(-19.8, 71.48) * mm});
            skLineSegment(sketch, "E55.direction1", {"start": v(-131.8, 71.1) * mm, "end": v(-131.5, 71.1) * mm, "construction": true});
            skLineSegment(sketch, "E55.direction2", {"start": v(-131.8, 71.1) * mm, "end": v(-131.8, 71.4) * mm, "construction": true});
            skSolve(sketch);
        }
        {
            var Q0;
            Q0 = qSketchRegion(id + "F4", true);
            extrude(context, id + "F5", {"entities" : qUnion([Q0]), "operationType" : NewBodyOperationType.ADD, "depth" : 1 * mm});
        }
        {
            var Q0;
            Q0=makeQuery(id+"F5.opExtrude","CAP_FACE",FACE,{"disambiguationData":[OSD([sQuery(id+"F4.wireOp",EDGE,"E55.1.1.0"),sQuery(id+"F4.wireOp",EDGE,"E55.1.1.1"),sQuery(id+"F4.wireOp",EDGE,"E55.1.1.2"),sQuery(id+"F4.wireOp",EDGE,"E55.1.1.3"),sQuery(id+"F4.wireOp",EDGE,"E55.1.1.4"),sQuery(id+"F4.wireOp",EDGE,"E55.1.1.5"),sQuery(id+"F4.wireOp",EDGE,"E55.1.1.6"),sQuery(id+"F4.wireOp",EDGE,"E55.1.1.7"),sQuery(id+"F4.wireOp",EDGE,"E55.1.1.8"),sQuery(id+"F4.wireOp",EDGE,"E55.1.1.9"),sQuery(id+"F4.wireOp",EDGE,"E55.1.1.10"),sQuery(id+"F4.wireOp",EDGE,"E55.1.1.11"),sQuery(id+"F4.wireOp",EDGE,"E55.1.1.12"),sQuery(id+"F4.wireOp",EDGE,"E55.1.1.13"),sQuery(id+"F4.wireOp",EDGE,"E55.1.1.14"),sQuery(id+"F4.wireOp",EDGE,"E55.1.1.15")])],"isStart":false});
            var sketch = newSketch(context, id + "F6", { "sketchPlane" : qUnion([Q0])});
            skArc(sketch, "E56.0", {"start": v(-131.2, 87.4) * mm, "mid": v(-113.55, 93.2) * mm, "end": v(-95.97, 87.21) * mm, "construction": true});
            skArc(sketch, "E56.1", {"start": v(-55.43, 87.21) * mm, "mid": v(-75.7, 80.37) * mm, "end": v(-95.97, 87.21) * mm, "construction": true});
            skArc(sketch, "E56.2", {"start": v(-55.43, 87.21) * mm, "mid": v(-37.7, 93.2) * mm, "end": v(-19.97, 87.21) * mm, "construction": true});
            skArc(sketch, "E56.3", {"start": v(20.57, 87.21) * mm, "mid": v(0.3, 80.37) * mm, "end": v(-19.97, 87.21) * mm, "construction": true});
            skArc(sketch, "E56.4", {"start": v(20.57, 87.21) * mm, "mid": v(38.3, 93.2) * mm, "end": v(56.03, 87.21) * mm, "construction": true});
            skArc(sketch, "E56.5", {"start": v(20.57, 71.72) * mm, "mid": v(0.3, 78.57) * mm, "end": v(-19.97, 71.72) * mm, "construction": true});
            skArc(sketch, "E56.6", {"start": v(-55.43, 71.72) * mm, "mid": v(-37.7, 65.73) * mm, "end": v(-19.97, 71.72) * mm, "construction": true});
            skArc(sketch, "E56.7", {"start": v(-55.43, 71.72) * mm, "mid": v(-75.7, 78.57) * mm, "end": v(-95.97, 71.72) * mm, "construction": true});
            skArc(sketch, "E56.8", {"start": v(-131.2, 71.54) * mm, "mid": v(-113.55, 65.73) * mm, "end": v(-95.97, 71.72) * mm, "construction": true});
            skArc(sketch, "E56.9", {"start": v(20.57, 71.72) * mm, "mid": v(38.3, 65.73) * mm, "end": v(56.03, 71.72) * mm, "construction": true});
            skArc(sketch, "E56.10", {"start": v(96.57, 71.72) * mm, "mid": v(76.3, 78.57) * mm, "end": v(56.03, 71.72) * mm, "construction": true});
            skArc(sketch, "E56.11", {"start": v(96.57, 71.72) * mm, "mid": v(114.15, 65.73) * mm, "end": v(131.8, 71.54) * mm, "construction": true});
            skLineSegment(sketch, "E56.12", {"start": v(131.8, 87.4) * mm, "end": v(131.8, 71.54) * mm, "construction": true});
            skArc(sketch, "E56.13", {"start": v(96.57, 87.21) * mm, "mid": v(114.15, 93.2) * mm, "end": v(131.8, 87.4) * mm, "construction": true});
            skLineSegment(sketch, "E56.14", {"start": v(-131.2, 87.4) * mm, "end": v(-131.2, 71.54) * mm, "construction": true});
            skArc(sketch, "E56.15", {"start": v(96.57, 87.21) * mm, "mid": v(76.3, 80.37) * mm, "end": v(56.03, 87.21) * mm, "construction": true});
            skArc(sketch, "E57.0.1.0", {"start": v(20.57, 87.51) * mm, "mid": v(0.3, 80.67) * mm, "end": v(-19.97, 87.51) * mm, "construction": true});
            skLineSegment(sketch, "E57.0.1.1", {"start": v(-131.2, 87.7) * mm, "end": v(-131.2, 71.84) * mm, "construction": true});
            skArc(sketch, "E57.0.1.2", {"start": v(-131.2, 71.84) * mm, "mid": v(-113.55, 66.03) * mm, "end": v(-95.97, 72.02) * mm, "construction": true});
            skArc(sketch, "E57.0.1.3", {"start": v(-55.43, 87.51) * mm, "mid": v(-37.7, 93.5) * mm, "end": v(-19.97, 87.51) * mm, "construction": true});
            skArc(sketch, "E57.0.1.4", {"start": v(96.57, 72.02) * mm, "mid": v(114.15, 66.03) * mm, "end": v(131.8, 71.84) * mm, "construction": true});
            skArc(sketch, "E57.0.1.5", {"start": v(-55.43, 72.02) * mm, "mid": v(-75.7, 78.87) * mm, "end": v(-95.97, 72.02) * mm, "construction": true});
            skArc(sketch, "E57.0.1.6", {"start": v(-55.43, 87.51) * mm, "mid": v(-75.7, 80.67) * mm, "end": v(-95.97, 87.51) * mm, "construction": true});
            skArc(sketch, "E57.0.1.7", {"start": v(96.57, 87.51) * mm, "mid": v(114.15, 93.5) * mm, "end": v(131.8, 87.7) * mm, "construction": true});
            skArc(sketch, "E57.0.1.8", {"start": v(-131.2, 87.7) * mm, "mid": v(-113.55, 93.5) * mm, "end": v(-95.97, 87.51) * mm, "construction": true});
            skArc(sketch, "E57.0.1.9", {"start": v(-55.43, 72.02) * mm, "mid": v(-37.7, 66.03) * mm, "end": v(-19.97, 72.02) * mm, "construction": true});
            skArc(sketch, "E57.0.1.10", {"start": v(20.57, 72.02) * mm, "mid": v(0.3, 78.87) * mm, "end": v(-19.97, 72.02) * mm, "construction": true});
            skArc(sketch, "E57.0.1.11", {"start": v(96.57, 72.02) * mm, "mid": v(76.3, 78.87) * mm, "end": v(56.03, 72.02) * mm, "construction": true});
            skArc(sketch, "E57.0.1.12", {"start": v(96.57, 87.51) * mm, "mid": v(76.3, 80.67) * mm, "end": v(56.03, 87.51) * mm, "construction": true});
            skArc(sketch, "E57.0.1.13", {"start": v(20.57, 87.51) * mm, "mid": v(38.3, 93.5) * mm, "end": v(56.03, 87.51) * mm, "construction": true});
            skLineSegment(sketch, "E57.0.1.14", {"start": v(131.8, 87.7) * mm, "end": v(131.8, 71.84) * mm, "construction": true});
            skArc(sketch, "E57.0.1.15", {"start": v(20.57, 72.02) * mm, "mid": v(38.3, 66.03) * mm, "end": v(56.03, 72.02) * mm, "construction": true});
            skArc(sketch, "E57.1.0.0", {"start": v(20.87, 87.21) * mm, "mid": v(0.6, 80.37) * mm, "end": v(-19.67, 87.21) * mm, "construction": true});
            skLineSegment(sketch, "E57.1.0.1", {"start": v(-130.9, 87.4) * mm, "end": v(-130.9, 71.54) * mm, "construction": true});
            skArc(sketch, "E57.1.0.2", {"start": v(-130.9, 71.54) * mm, "mid": v(-113.25, 65.73) * mm, "end": v(-95.67, 71.72) * mm, "construction": true});
            skArc(sketch, "E57.1.0.3", {"start": v(-55.13, 87.21) * mm, "mid": v(-37.4, 93.2) * mm, "end": v(-19.67, 87.21) * mm, "construction": true});
            skArc(sketch, "E57.1.0.4", {"start": v(96.87, 71.72) * mm, "mid": v(114.45, 65.73) * mm, "end": v(132.1, 71.54) * mm, "construction": true});
            skArc(sketch, "E57.1.0.5", {"start": v(-55.13, 71.72) * mm, "mid": v(-75.4, 78.57) * mm, "end": v(-95.67, 71.72) * mm, "construction": true});
            skArc(sketch, "E57.1.0.6", {"start": v(-55.13, 87.21) * mm, "mid": v(-75.4, 80.37) * mm, "end": v(-95.67, 87.21) * mm, "construction": true});
            skArc(sketch, "E57.1.0.7", {"start": v(96.87, 87.21) * mm, "mid": v(114.45, 93.2) * mm, "end": v(132.1, 87.4) * mm, "construction": true});
            skArc(sketch, "E57.1.0.8", {"start": v(-130.9, 87.4) * mm, "mid": v(-113.25, 93.2) * mm, "end": v(-95.67, 87.21) * mm, "construction": true});
            skArc(sketch, "E57.1.0.9", {"start": v(-55.13, 71.72) * mm, "mid": v(-37.4, 65.73) * mm, "end": v(-19.67, 71.72) * mm, "construction": true});
            skArc(sketch, "E57.1.0.10", {"start": v(20.87, 71.72) * mm, "mid": v(0.6, 78.57) * mm, "end": v(-19.67, 71.72) * mm, "construction": true});
            skArc(sketch, "E57.1.0.11", {"start": v(96.87, 71.72) * mm, "mid": v(76.6, 78.57) * mm, "end": v(56.33, 71.72) * mm, "construction": true});
            skArc(sketch, "E57.1.0.12", {"start": v(96.87, 87.21) * mm, "mid": v(76.6, 80.37) * mm, "end": v(56.33, 87.21) * mm, "construction": true});
            skArc(sketch, "E57.1.0.13", {"start": v(20.87, 87.21) * mm, "mid": v(38.6, 93.2) * mm, "end": v(56.33, 87.21) * mm, "construction": true});
            skLineSegment(sketch, "E57.1.0.14", {"start": v(132.1, 87.4) * mm, "end": v(132.1, 71.54) * mm, "construction": true});
            skArc(sketch, "E57.1.0.15", {"start": v(20.87, 71.72) * mm, "mid": v(38.6, 65.73) * mm, "end": v(56.33, 71.72) * mm, "construction": true});
            skArc(sketch, "E57.1.1.0", {"start": v(20.87, 87.51) * mm, "mid": v(0.6, 80.67) * mm, "end": v(-19.67, 87.51) * mm});
            skLineSegment(sketch, "E57.1.1.1", {"start": v(-130.9, 87.7) * mm, "end": v(-130.9, 71.84) * mm});
            skArc(sketch, "E57.1.1.2", {"start": v(-130.9, 71.84) * mm, "mid": v(-113.25, 66.03) * mm, "end": v(-95.67, 72.02) * mm});
            skArc(sketch, "E57.1.1.3", {"start": v(-55.13, 87.51) * mm, "mid": v(-37.4, 93.5) * mm, "end": v(-19.67, 87.51) * mm});
            skArc(sketch, "E57.1.1.4", {"start": v(96.87, 72.02) * mm, "mid": v(114.45, 66.03) * mm, "end": v(132.1, 71.84) * mm});
            skArc(sketch, "E57.1.1.5", {"start": v(-55.13, 72.02) * mm, "mid": v(-75.4, 78.87) * mm, "end": v(-95.67, 72.02) * mm});
            skArc(sketch, "E57.1.1.6", {"start": v(-55.13, 87.51) * mm, "mid": v(-75.4, 80.67) * mm, "end": v(-95.67, 87.51) * mm});
            skArc(sketch, "E57.1.1.7", {"start": v(96.87, 87.51) * mm, "mid": v(114.45, 93.5) * mm, "end": v(132.1, 87.7) * mm});
            skArc(sketch, "E57.1.1.8", {"start": v(-130.9, 87.7) * mm, "mid": v(-113.25, 93.5) * mm, "end": v(-95.67, 87.51) * mm});
            skArc(sketch, "E57.1.1.9", {"start": v(-55.13, 72.02) * mm, "mid": v(-37.4, 66.03) * mm, "end": v(-19.67, 72.02) * mm});
            skArc(sketch, "E57.1.1.10", {"start": v(20.87, 72.02) * mm, "mid": v(0.6, 78.87) * mm, "end": v(-19.67, 72.02) * mm});
            skArc(sketch, "E57.1.1.11", {"start": v(96.87, 72.02) * mm, "mid": v(76.6, 78.87) * mm, "end": v(56.33, 72.02) * mm});
            skArc(sketch, "E57.1.1.12", {"start": v(96.87, 87.51) * mm, "mid": v(76.6, 80.67) * mm, "end": v(56.33, 87.51) * mm});
            skArc(sketch, "E57.1.1.13", {"start": v(20.87, 87.51) * mm, "mid": v(38.6, 93.5) * mm, "end": v(56.33, 87.51) * mm});
            skLineSegment(sketch, "E57.1.1.14", {"start": v(132.1, 87.7) * mm, "end": v(132.1, 71.84) * mm});
            skArc(sketch, "E57.1.1.15", {"start": v(20.87, 72.02) * mm, "mid": v(38.6, 66.03) * mm, "end": v(56.33, 72.02) * mm});
            skLineSegment(sketch, "E57.direction1", {"start": v(-131.2, 71.54) * mm, "end": v(-130.9, 71.54) * mm, "construction": true});
            skLineSegment(sketch, "E57.direction2", {"start": v(-131.2, 71.54) * mm, "end": v(-131.2, 71.84) * mm, "construction": true});
            skSolve(sketch);
        }
        {
            var Q0;
            Q0 = qSketchRegion(id + "F6", true);
            extrude(context, id + "F7", {"entities" : qUnion([Q0]), "operationType" : NewBodyOperationType.ADD, "depth" : 1 * mm});
        }
        {
            var Q0;
            Q0=makeQuery(id+"F7.opExtrude","CAP_FACE",FACE,{"disambiguationData":[OSD([sQuery(id+"F6.wireOp",EDGE,"E57.1.1.0"),sQuery(id+"F6.wireOp",EDGE,"E57.1.1.1"),sQuery(id+"F6.wireOp",EDGE,"E57.1.1.2"),sQuery(id+"F6.wireOp",EDGE,"E57.1.1.3"),sQuery(id+"F6.wireOp",EDGE,"E57.1.1.4"),sQuery(id+"F6.wireOp",EDGE,"E57.1.1.5"),sQuery(id+"F6.wireOp",EDGE,"E57.1.1.6"),sQuery(id+"F6.wireOp",EDGE,"E57.1.1.7"),sQuery(id+"F6.wireOp",EDGE,"E57.1.1.8"),sQuery(id+"F6.wireOp",EDGE,"E57.1.1.9"),sQuery(id+"F6.wireOp",EDGE,"E57.1.1.10"),sQuery(id+"F6.wireOp",EDGE,"E57.1.1.11"),sQuery(id+"F6.wireOp",EDGE,"E57.1.1.12"),sQuery(id+"F6.wireOp",EDGE,"E57.1.1.13"),sQuery(id+"F6.wireOp",EDGE,"E57.1.1.14"),sQuery(id+"F6.wireOp",EDGE,"E57.1.1.15")])],"isStart":false});
            var sketch = newSketch(context, id + "F8", { "sketchPlane" : qUnion([Q0])});
            skArc(sketch, "E58.0", {"start": v(-130.6, 87.54) * mm, "mid": v(-113.18, 93.2) * mm, "end": v(-95.86, 87.27) * mm, "construction": true});
            skArc(sketch, "E58.1", {"start": v(-54.94, 87.27) * mm, "mid": v(-75.4, 80.37) * mm, "end": v(-95.86, 87.27) * mm, "construction": true});
            skArc(sketch, "E58.2", {"start": v(-54.94, 87.27) * mm, "mid": v(-37.4, 93.2) * mm, "end": v(-19.86, 87.27) * mm, "construction": true});
            skArc(sketch, "E58.3", {"start": v(21.06, 87.27) * mm, "mid": v(0.6, 80.37) * mm, "end": v(-19.86, 87.27) * mm, "construction": true});
            skArc(sketch, "E58.4", {"start": v(21.06, 87.27) * mm, "mid": v(38.6, 93.2) * mm, "end": v(56.14, 87.27) * mm, "construction": true});
            skArc(sketch, "E58.5", {"start": v(21.06, 72.26) * mm, "mid": v(0.6, 79.17) * mm, "end": v(-19.86, 72.26) * mm, "construction": true});
            skArc(sketch, "E58.6", {"start": v(-54.94, 72.26) * mm, "mid": v(-37.4, 66.33) * mm, "end": v(-19.86, 72.26) * mm, "construction": true});
            skArc(sketch, "E58.7", {"start": v(-54.94, 72.26) * mm, "mid": v(-75.4, 79.17) * mm, "end": v(-95.86, 72.26) * mm, "construction": true});
            skArc(sketch, "E58.8", {"start": v(-130.6, 72) * mm, "mid": v(-113.18, 66.33) * mm, "end": v(-95.86, 72.26) * mm, "construction": true});
            skArc(sketch, "E58.9", {"start": v(21.06, 72.26) * mm, "mid": v(38.6, 66.33) * mm, "end": v(56.14, 72.26) * mm, "construction": true});
            skArc(sketch, "E58.10", {"start": v(97.06, 72.26) * mm, "mid": v(76.6, 79.17) * mm, "end": v(56.14, 72.26) * mm, "construction": true});
            skArc(sketch, "E58.11", {"start": v(97.06, 72.26) * mm, "mid": v(114.38, 66.33) * mm, "end": v(131.8, 72) * mm, "construction": true});
            skLineSegment(sketch, "E58.12", {"start": v(131.8, 87.54) * mm, "end": v(131.8, 72) * mm, "construction": true});
            skArc(sketch, "E58.13", {"start": v(97.06, 87.27) * mm, "mid": v(114.38, 93.2) * mm, "end": v(131.8, 87.54) * mm, "construction": true});
            skLineSegment(sketch, "E58.14", {"start": v(-130.6, 87.54) * mm, "end": v(-130.6, 72) * mm, "construction": true});
            skArc(sketch, "E58.15", {"start": v(97.06, 87.27) * mm, "mid": v(76.6, 80.37) * mm, "end": v(56.14, 87.27) * mm, "construction": true});
            skArc(sketch, "E59.0.1.0", {"start": v(21.06, 87.57) * mm, "mid": v(38.6, 93.5) * mm, "end": v(56.14, 87.57) * mm, "construction": true});
            skArc(sketch, "E59.0.1.1", {"start": v(97.06, 72.56) * mm, "mid": v(114.38, 66.63) * mm, "end": v(131.8, 72.3) * mm, "construction": true});
            skArc(sketch, "E59.0.1.2", {"start": v(21.06, 72.56) * mm, "mid": v(38.6, 66.63) * mm, "end": v(56.14, 72.56) * mm, "construction": true});
            skArc(sketch, "E59.0.1.3", {"start": v(21.06, 87.57) * mm, "mid": v(0.6, 80.67) * mm, "end": v(-19.86, 87.57) * mm, "construction": true});
            skArc(sketch, "E59.0.1.4", {"start": v(97.06, 87.57) * mm, "mid": v(114.38, 93.5) * mm, "end": v(131.8, 87.84) * mm, "construction": true});
            skArc(sketch, "E59.0.1.5", {"start": v(-130.6, 72.3) * mm, "mid": v(-113.18, 66.63) * mm, "end": v(-95.86, 72.56) * mm, "construction": true});
            skArc(sketch, "E59.0.1.6", {"start": v(-54.94, 87.57) * mm, "mid": v(-37.4, 93.5) * mm, "end": v(-19.86, 87.57) * mm, "construction": true});
            skArc(sketch, "E59.0.1.7", {"start": v(-54.94, 72.56) * mm, "mid": v(-75.4, 79.47) * mm, "end": v(-95.86, 72.56) * mm, "construction": true});
            skArc(sketch, "E59.0.1.8", {"start": v(97.06, 87.57) * mm, "mid": v(76.6, 80.67) * mm, "end": v(56.14, 87.57) * mm, "construction": true});
            skArc(sketch, "E59.0.1.9", {"start": v(-54.94, 87.57) * mm, "mid": v(-75.4, 80.67) * mm, "end": v(-95.86, 87.57) * mm, "construction": true});
            skArc(sketch, "E59.0.1.10", {"start": v(97.06, 72.56) * mm, "mid": v(76.6, 79.47) * mm, "end": v(56.14, 72.56) * mm, "construction": true});
            skArc(sketch, "E59.0.1.11", {"start": v(-54.94, 72.56) * mm, "mid": v(-37.4, 66.63) * mm, "end": v(-19.86, 72.56) * mm, "construction": true});
            skArc(sketch, "E59.0.1.12", {"start": v(-130.6, 87.84) * mm, "mid": v(-113.18, 93.5) * mm, "end": v(-95.86, 87.57) * mm, "construction": true});
            skLineSegment(sketch, "E59.0.1.13", {"start": v(131.8, 87.84) * mm, "end": v(131.8, 72.3) * mm, "construction": true});
            skArc(sketch, "E59.0.1.14", {"start": v(21.06, 72.56) * mm, "mid": v(0.6, 79.47) * mm, "end": v(-19.86, 72.56) * mm, "construction": true});
            skLineSegment(sketch, "E59.0.1.15", {"start": v(-130.6, 87.84) * mm, "end": v(-130.6, 72.3) * mm, "construction": true});
            skArc(sketch, "E59.1.0.0", {"start": v(21.36, 87.27) * mm, "mid": v(38.9, 93.2) * mm, "end": v(56.44, 87.27) * mm, "construction": true});
            skArc(sketch, "E59.1.0.1", {"start": v(97.36, 72.26) * mm, "mid": v(114.68, 66.33) * mm, "end": v(132.1, 72) * mm, "construction": true});
            skArc(sketch, "E59.1.0.2", {"start": v(21.36, 72.26) * mm, "mid": v(38.9, 66.33) * mm, "end": v(56.44, 72.26) * mm, "construction": true});
            skArc(sketch, "E59.1.0.3", {"start": v(21.36, 87.27) * mm, "mid": v(0.9, 80.37) * mm, "end": v(-19.56, 87.27) * mm, "construction": true});
            skArc(sketch, "E59.1.0.4", {"start": v(97.36, 87.27) * mm, "mid": v(114.68, 93.2) * mm, "end": v(132.1, 87.54) * mm, "construction": true});
            skArc(sketch, "E59.1.0.5", {"start": v(-130.3, 72) * mm, "mid": v(-112.88, 66.33) * mm, "end": v(-95.56, 72.26) * mm, "construction": true});
            skArc(sketch, "E59.1.0.6", {"start": v(-54.64, 87.27) * mm, "mid": v(-37.1, 93.2) * mm, "end": v(-19.56, 87.27) * mm, "construction": true});
            skArc(sketch, "E59.1.0.7", {"start": v(-54.64, 72.26) * mm, "mid": v(-75.1, 79.17) * mm, "end": v(-95.56, 72.26) * mm, "construction": true});
            skArc(sketch, "E59.1.0.8", {"start": v(97.36, 87.27) * mm, "mid": v(76.9, 80.37) * mm, "end": v(56.44, 87.27) * mm, "construction": true});
            skArc(sketch, "E59.1.0.9", {"start": v(-54.64, 87.27) * mm, "mid": v(-75.1, 80.37) * mm, "end": v(-95.56, 87.27) * mm, "construction": true});
            skArc(sketch, "E59.1.0.10", {"start": v(97.36, 72.26) * mm, "mid": v(76.9, 79.17) * mm, "end": v(56.44, 72.26) * mm, "construction": true});
            skArc(sketch, "E59.1.0.11", {"start": v(-54.64, 72.26) * mm, "mid": v(-37.1, 66.33) * mm, "end": v(-19.56, 72.26) * mm, "construction": true});
            skArc(sketch, "E59.1.0.12", {"start": v(-130.3, 87.54) * mm, "mid": v(-112.88, 93.2) * mm, "end": v(-95.56, 87.27) * mm, "construction": true});
            skLineSegment(sketch, "E59.1.0.13", {"start": v(132.1, 87.54) * mm, "end": v(132.1, 72) * mm, "construction": true});
            skArc(sketch, "E59.1.0.14", {"start": v(21.36, 72.26) * mm, "mid": v(0.9, 79.17) * mm, "end": v(-19.56, 72.26) * mm, "construction": true});
            skLineSegment(sketch, "E59.1.0.15", {"start": v(-130.3, 87.54) * mm, "end": v(-130.3, 72) * mm, "construction": true});
            skArc(sketch, "E59.1.1.0", {"start": v(21.36, 87.57) * mm, "mid": v(38.9, 93.5) * mm, "end": v(56.44, 87.57) * mm});
            skArc(sketch, "E59.1.1.1", {"start": v(97.36, 72.56) * mm, "mid": v(114.68, 66.63) * mm, "end": v(132.1, 72.3) * mm});
            skArc(sketch, "E59.1.1.2", {"start": v(21.36, 72.56) * mm, "mid": v(38.9, 66.63) * mm, "end": v(56.44, 72.56) * mm});
            skArc(sketch, "E59.1.1.3", {"start": v(21.36, 87.57) * mm, "mid": v(0.9, 80.67) * mm, "end": v(-19.56, 87.57) * mm});
            skArc(sketch, "E59.1.1.4", {"start": v(97.36, 87.57) * mm, "mid": v(114.68, 93.5) * mm, "end": v(132.1, 87.84) * mm});
            skArc(sketch, "E59.1.1.5", {"start": v(-130.3, 72.3) * mm, "mid": v(-112.88, 66.63) * mm, "end": v(-95.56, 72.56) * mm});
            skArc(sketch, "E59.1.1.6", {"start": v(-54.64, 87.57) * mm, "mid": v(-37.1, 93.5) * mm, "end": v(-19.56, 87.57) * mm});
            skArc(sketch, "E59.1.1.7", {"start": v(-54.64, 72.56) * mm, "mid": v(-75.1, 79.47) * mm, "end": v(-95.56, 72.56) * mm});
            skArc(sketch, "E59.1.1.8", {"start": v(97.36, 87.57) * mm, "mid": v(76.9, 80.67) * mm, "end": v(56.44, 87.57) * mm});
            skArc(sketch, "E59.1.1.9", {"start": v(-54.64, 87.57) * mm, "mid": v(-75.1, 80.67) * mm, "end": v(-95.56, 87.57) * mm});
            skArc(sketch, "E59.1.1.10", {"start": v(97.36, 72.56) * mm, "mid": v(76.9, 79.47) * mm, "end": v(56.44, 72.56) * mm});
            skArc(sketch, "E59.1.1.11", {"start": v(-54.64, 72.56) * mm, "mid": v(-37.1, 66.63) * mm, "end": v(-19.56, 72.56) * mm});
            skArc(sketch, "E59.1.1.12", {"start": v(-130.3, 87.84) * mm, "mid": v(-112.88, 93.5) * mm, "end": v(-95.56, 87.57) * mm});
            skLineSegment(sketch, "E59.1.1.13", {"start": v(132.1, 87.84) * mm, "end": v(132.1, 72.3) * mm});
            skArc(sketch, "E59.1.1.14", {"start": v(21.36, 72.56) * mm, "mid": v(0.9, 79.47) * mm, "end": v(-19.56, 72.56) * mm});
            skLineSegment(sketch, "E59.1.1.15", {"start": v(-130.3, 87.84) * mm, "end": v(-130.3, 72.3) * mm});
            skLineSegment(sketch, "E59.direction1", {"start": v(-130.6, 72) * mm, "end": v(-130.3, 72) * mm, "construction": true});
            skLineSegment(sketch, "E59.direction2", {"start": v(-130.6, 72) * mm, "end": v(-130.6, 72.3) * mm, "construction": true});
            skSolve(sketch);
        }
        {
            var Q0;
            Q0 = qSketchRegion(id + "F8", true);
            extrude(context, id + "F9", {"entities" : qUnion([Q0]), "operationType" : NewBodyOperationType.ADD, "depth" : 1 * mm});
        }
        {
            var Q0;
            Q0=makeQuery(id+"F9.opExtrude","CAP_FACE",FACE,{"disambiguationData":[OSD([sQuery(id+"F8.wireOp",EDGE,"E59.1.1.0"),sQuery(id+"F8.wireOp",EDGE,"E59.1.1.1"),sQuery(id+"F8.wireOp",EDGE,"E59.1.1.2"),sQuery(id+"F8.wireOp",EDGE,"E59.1.1.3"),sQuery(id+"F8.wireOp",EDGE,"E59.1.1.4"),sQuery(id+"F8.wireOp",EDGE,"E59.1.1.5"),sQuery(id+"F8.wireOp",EDGE,"E59.1.1.6"),sQuery(id+"F8.wireOp",EDGE,"E59.1.1.7"),sQuery(id+"F8.wireOp",EDGE,"E59.1.1.8"),sQuery(id+"F8.wireOp",EDGE,"E59.1.1.9"),sQuery(id+"F8.wireOp",EDGE,"E59.1.1.10"),sQuery(id+"F8.wireOp",EDGE,"E59.1.1.11"),sQuery(id+"F8.wireOp",EDGE,"E59.1.1.12"),sQuery(id+"F8.wireOp",EDGE,"E59.1.1.13"),sQuery(id+"F8.wireOp",EDGE,"E59.1.1.14"),sQuery(id+"F8.wireOp",EDGE,"E59.1.1.15")])],"isStart":false});
            var sketch = newSketch(context, id + "F10", { "sketchPlane" : qUnion([Q0])});
            skArc(sketch, "E60.0", {"start": v(-130, 87.69) * mm, "mid": v(-112.8, 93.2) * mm, "end": v(-95.74, 87.34) * mm, "construction": true});
            skArc(sketch, "E60.1", {"start": v(-54.46, 87.34) * mm, "mid": v(-75.1, 80.37) * mm, "end": v(-95.74, 87.34) * mm, "construction": true});
            skArc(sketch, "E60.2", {"start": v(-54.46, 87.34) * mm, "mid": v(-37.1, 93.2) * mm, "end": v(-19.74, 87.34) * mm, "construction": true});
            skArc(sketch, "E60.3", {"start": v(21.54, 87.34) * mm, "mid": v(0.9, 80.37) * mm, "end": v(-19.74, 87.34) * mm, "construction": true});
            skArc(sketch, "E60.4", {"start": v(21.54, 87.34) * mm, "mid": v(38.9, 93.2) * mm, "end": v(56.26, 87.34) * mm, "construction": true});
            skArc(sketch, "E60.5", {"start": v(21.54, 72.8) * mm, "mid": v(0.9, 79.77) * mm, "end": v(-19.74, 72.8) * mm, "construction": true});
            skArc(sketch, "E60.6", {"start": v(-54.46, 72.8) * mm, "mid": v(-37.1, 66.93) * mm, "end": v(-19.74, 72.8) * mm, "construction": true});
            skArc(sketch, "E60.7", {"start": v(-54.46, 72.8) * mm, "mid": v(-75.1, 79.77) * mm, "end": v(-95.74, 72.8) * mm, "construction": true});
            skArc(sketch, "E60.8", {"start": v(-130, 72.44) * mm, "mid": v(-112.8, 66.93) * mm, "end": v(-95.74, 72.8) * mm, "construction": true});
            skArc(sketch, "E60.9", {"start": v(21.54, 72.8) * mm, "mid": v(38.9, 66.93) * mm, "end": v(56.26, 72.8) * mm, "construction": true});
            skArc(sketch, "E60.10", {"start": v(97.54, 72.8) * mm, "mid": v(76.9, 79.77) * mm, "end": v(56.26, 72.8) * mm, "construction": true});
            skArc(sketch, "E60.11", {"start": v(97.54, 72.8) * mm, "mid": v(114.6, 66.93) * mm, "end": v(131.8, 72.44) * mm, "construction": true});
            skLineSegment(sketch, "E60.12", {"start": v(131.8, 87.69) * mm, "end": v(131.8, 72.44) * mm, "construction": true});
            skArc(sketch, "E60.13", {"start": v(97.54, 87.34) * mm, "mid": v(114.6, 93.2) * mm, "end": v(131.8, 87.69) * mm, "construction": true});
            skLineSegment(sketch, "E60.14", {"start": v(-130, 87.69) * mm, "end": v(-130, 72.44) * mm, "construction": true});
            skArc(sketch, "E60.15", {"start": v(97.54, 87.34) * mm, "mid": v(76.9, 80.37) * mm, "end": v(56.26, 87.34) * mm, "construction": true});
            skArc(sketch, "E61.0.1.0", {"start": v(-54.46, 87.64) * mm, "mid": v(-37.1, 93.5) * mm, "end": v(-19.74, 87.64) * mm, "construction": true});
            skArc(sketch, "E61.0.1.1", {"start": v(97.54, 73.1) * mm, "mid": v(114.6, 67.23) * mm, "end": v(131.8, 72.74) * mm, "construction": true});
            skArc(sketch, "E61.0.1.2", {"start": v(-54.46, 73.1) * mm, "mid": v(-75.1, 80.07) * mm, "end": v(-95.74, 73.1) * mm, "construction": true});
            skArc(sketch, "E61.0.1.3", {"start": v(-54.46, 87.64) * mm, "mid": v(-75.1, 80.67) * mm, "end": v(-95.74, 87.64) * mm, "construction": true});
            skArc(sketch, "E61.0.1.4", {"start": v(97.54, 87.64) * mm, "mid": v(114.6, 93.5) * mm, "end": v(131.8, 87.99) * mm, "construction": true});
            skArc(sketch, "E61.0.1.5", {"start": v(-54.46, 73.1) * mm, "mid": v(-37.1, 67.23) * mm, "end": v(-19.74, 73.1) * mm, "construction": true});
            skArc(sketch, "E61.0.1.6", {"start": v(-130, 87.99) * mm, "mid": v(-112.8, 93.5) * mm, "end": v(-95.74, 87.64) * mm, "construction": true});
            skArc(sketch, "E61.0.1.7", {"start": v(97.54, 73.1) * mm, "mid": v(76.9, 80.07) * mm, "end": v(56.26, 73.1) * mm, "construction": true});
            skArc(sketch, "E61.0.1.8", {"start": v(97.54, 87.64) * mm, "mid": v(76.9, 80.67) * mm, "end": v(56.26, 87.64) * mm, "construction": true});
            skArc(sketch, "E61.0.1.9", {"start": v(21.54, 73.1) * mm, "mid": v(0.9, 80.07) * mm, "end": v(-19.74, 73.1) * mm, "construction": true});
            skLineSegment(sketch, "E61.0.1.10", {"start": v(131.8, 87.99) * mm, "end": v(131.8, 72.74) * mm, "construction": true});
            skArc(sketch, "E61.0.1.11", {"start": v(21.54, 87.64) * mm, "mid": v(38.9, 93.5) * mm, "end": v(56.26, 87.64) * mm, "construction": true});
            skArc(sketch, "E61.0.1.12", {"start": v(21.54, 73.1) * mm, "mid": v(38.9, 67.23) * mm, "end": v(56.26, 73.1) * mm, "construction": true});
            skArc(sketch, "E61.0.1.13", {"start": v(21.54, 87.64) * mm, "mid": v(0.9, 80.67) * mm, "end": v(-19.74, 87.64) * mm, "construction": true});
            skLineSegment(sketch, "E61.0.1.14", {"start": v(-130, 87.99) * mm, "end": v(-130, 72.74) * mm, "construction": true});
            skArc(sketch, "E61.0.1.15", {"start": v(-130, 72.74) * mm, "mid": v(-112.8, 67.23) * mm, "end": v(-95.74, 73.1) * mm, "construction": true});
            skArc(sketch, "E61.1.0.0", {"start": v(-54.16, 87.34) * mm, "mid": v(-36.8, 93.2) * mm, "end": v(-19.44, 87.34) * mm, "construction": true});
            skArc(sketch, "E61.1.0.1", {"start": v(97.84, 72.8) * mm, "mid": v(114.9, 66.93) * mm, "end": v(132.1, 72.44) * mm, "construction": true});
            skArc(sketch, "E61.1.0.2", {"start": v(-54.16, 72.8) * mm, "mid": v(-74.8, 79.77) * mm, "end": v(-95.44, 72.8) * mm, "construction": true});
            skArc(sketch, "E61.1.0.3", {"start": v(-54.16, 87.34) * mm, "mid": v(-74.8, 80.37) * mm, "end": v(-95.44, 87.34) * mm, "construction": true});
            skArc(sketch, "E61.1.0.4", {"start": v(97.84, 87.34) * mm, "mid": v(114.9, 93.2) * mm, "end": v(132.1, 87.69) * mm, "construction": true});
            skArc(sketch, "E61.1.0.5", {"start": v(-54.16, 72.8) * mm, "mid": v(-36.8, 66.93) * mm, "end": v(-19.44, 72.8) * mm, "construction": true});
            skArc(sketch, "E61.1.0.6", {"start": v(-129.7, 87.69) * mm, "mid": v(-112.5, 93.2) * mm, "end": v(-95.44, 87.34) * mm, "construction": true});
            skArc(sketch, "E61.1.0.7", {"start": v(97.84, 72.8) * mm, "mid": v(77.2, 79.77) * mm, "end": v(56.56, 72.8) * mm, "construction": true});
            skArc(sketch, "E61.1.0.8", {"start": v(97.84, 87.34) * mm, "mid": v(77.2, 80.37) * mm, "end": v(56.56, 87.34) * mm, "construction": true});
            skArc(sketch, "E61.1.0.9", {"start": v(21.84, 72.8) * mm, "mid": v(1.2, 79.77) * mm, "end": v(-19.44, 72.8) * mm, "construction": true});
            skLineSegment(sketch, "E61.1.0.10", {"start": v(132.1, 87.69) * mm, "end": v(132.1, 72.44) * mm, "construction": true});
            skArc(sketch, "E61.1.0.11", {"start": v(21.84, 87.34) * mm, "mid": v(39.2, 93.2) * mm, "end": v(56.56, 87.34) * mm, "construction": true});
            skArc(sketch, "E61.1.0.12", {"start": v(21.84, 72.8) * mm, "mid": v(39.2, 66.93) * mm, "end": v(56.56, 72.8) * mm, "construction": true});
            skArc(sketch, "E61.1.0.13", {"start": v(21.84, 87.34) * mm, "mid": v(1.2, 80.37) * mm, "end": v(-19.44, 87.34) * mm, "construction": true});
            skLineSegment(sketch, "E61.1.0.14", {"start": v(-129.7, 87.69) * mm, "end": v(-129.7, 72.44) * mm, "construction": true});
            skArc(sketch, "E61.1.0.15", {"start": v(-129.7, 72.44) * mm, "mid": v(-112.5, 66.93) * mm, "end": v(-95.44, 72.8) * mm, "construction": true});
            skArc(sketch, "E61.1.1.0", {"start": v(-54.16, 87.64) * mm, "mid": v(-36.8, 93.5) * mm, "end": v(-19.44, 87.64) * mm});
            skArc(sketch, "E61.1.1.1", {"start": v(97.84, 73.1) * mm, "mid": v(114.9, 67.23) * mm, "end": v(132.1, 72.74) * mm});
            skArc(sketch, "E61.1.1.2", {"start": v(-54.16, 73.1) * mm, "mid": v(-74.8, 80.07) * mm, "end": v(-95.44, 73.1) * mm});
            skArc(sketch, "E61.1.1.3", {"start": v(-54.16, 87.64) * mm, "mid": v(-74.8, 80.67) * mm, "end": v(-95.44, 87.64) * mm});
            skArc(sketch, "E61.1.1.4", {"start": v(97.84, 87.64) * mm, "mid": v(114.9, 93.5) * mm, "end": v(132.1, 87.99) * mm});
            skArc(sketch, "E61.1.1.5", {"start": v(-54.16, 73.1) * mm, "mid": v(-36.8, 67.23) * mm, "end": v(-19.44, 73.1) * mm});
            skArc(sketch, "E61.1.1.6", {"start": v(-129.7, 87.99) * mm, "mid": v(-112.5, 93.5) * mm, "end": v(-95.44, 87.64) * mm});
            skArc(sketch, "E61.1.1.7", {"start": v(97.84, 73.1) * mm, "mid": v(77.2, 80.07) * mm, "end": v(56.56, 73.1) * mm});
            skArc(sketch, "E61.1.1.8", {"start": v(97.84, 87.64) * mm, "mid": v(77.2, 80.67) * mm, "end": v(56.56, 87.64) * mm});
            skArc(sketch, "E61.1.1.9", {"start": v(21.84, 73.1) * mm, "mid": v(1.2, 80.07) * mm, "end": v(-19.44, 73.1) * mm});
            skLineSegment(sketch, "E61.1.1.10", {"start": v(132.1, 87.99) * mm, "end": v(132.1, 72.74) * mm});
            skArc(sketch, "E61.1.1.11", {"start": v(21.84, 87.64) * mm, "mid": v(39.2, 93.5) * mm, "end": v(56.56, 87.64) * mm});
            skArc(sketch, "E61.1.1.12", {"start": v(21.84, 73.1) * mm, "mid": v(39.2, 67.23) * mm, "end": v(56.56, 73.1) * mm});
            skArc(sketch, "E61.1.1.13", {"start": v(21.84, 87.64) * mm, "mid": v(1.2, 80.67) * mm, "end": v(-19.44, 87.64) * mm});
            skLineSegment(sketch, "E61.1.1.14", {"start": v(-129.7, 87.99) * mm, "end": v(-129.7, 72.74) * mm});
            skArc(sketch, "E61.1.1.15", {"start": v(-129.7, 72.74) * mm, "mid": v(-112.5, 67.23) * mm, "end": v(-95.44, 73.1) * mm});
            skLineSegment(sketch, "E61.direction1", {"start": v(-130, 72.44) * mm, "end": v(-129.7, 72.44) * mm, "construction": true});
            skLineSegment(sketch, "E61.direction2", {"start": v(-130, 72.44) * mm, "end": v(-130, 72.74) * mm, "construction": true});
            skSolve(sketch);
        }
        {
            var Q0;
            Q0 = qSketchRegion(id + "F10", true);
            extrude(context, id + "F11", {"entities" : qUnion([Q0]), "operationType" : NewBodyOperationType.ADD, "depth" : 1 * mm});
        }
    });
